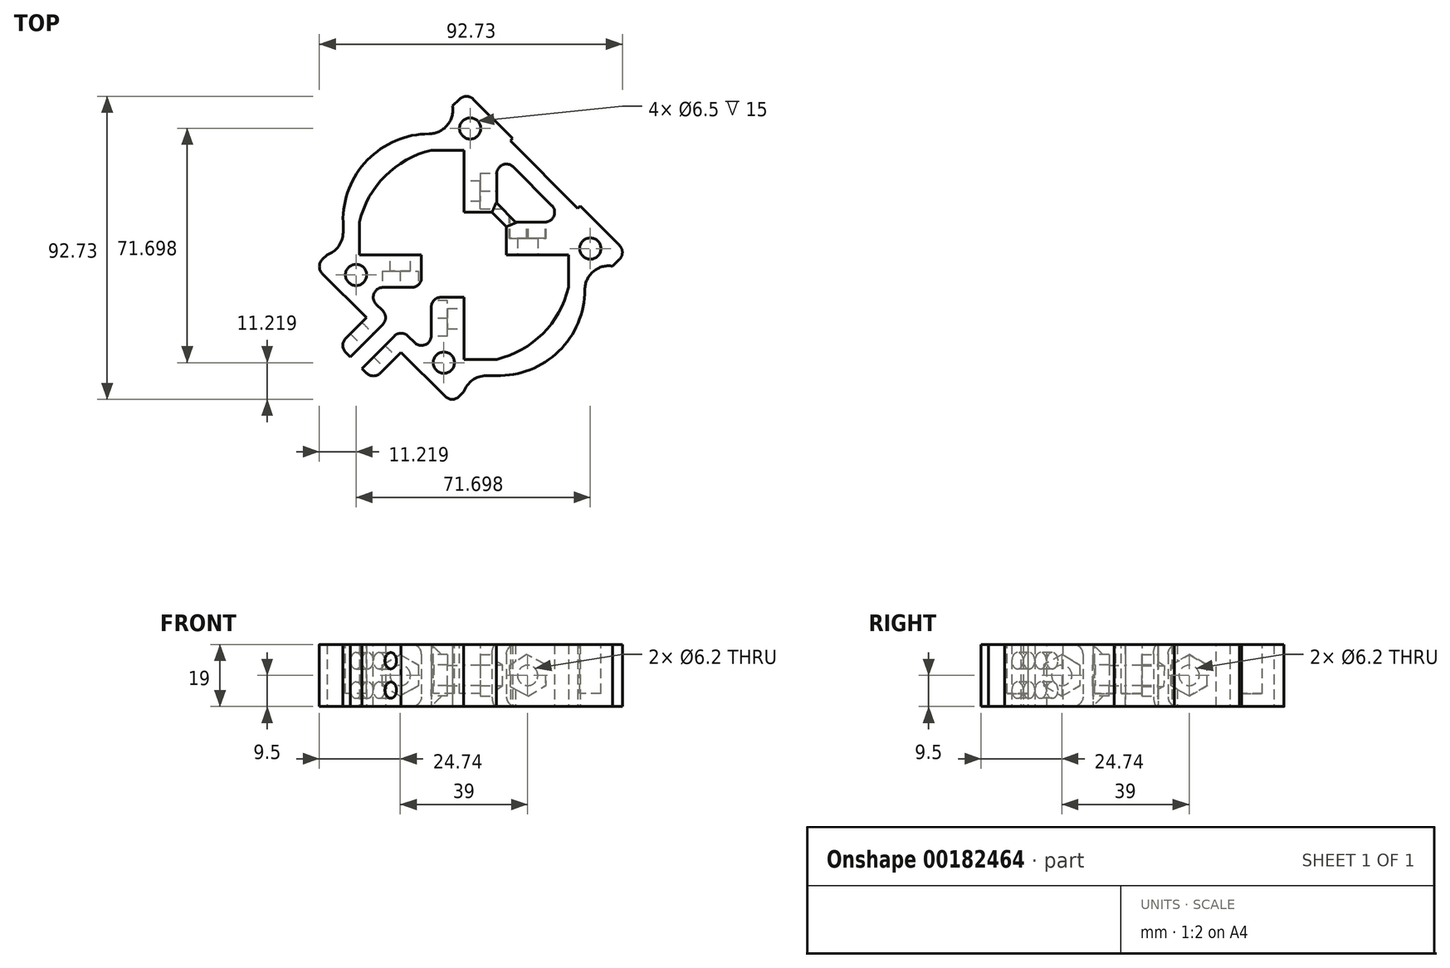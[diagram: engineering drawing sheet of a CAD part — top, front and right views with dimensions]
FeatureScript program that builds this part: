
annotation { "Feature Type Name" : "Feature", "Feature Type Description" : "" }
export const myFeature = defineFeature(function(context is Context, id is Id, definition is map)
    precondition{}
    {
        {
            var Q0;
            Q0=qCreatedBy(makeId("Top.planeOp"),FACE);
            var sketch = newSketch(context, id + "F0", { "sketchPlane" : qUnion([Q0])});
            skLineSegment(sketch, "E0.bottom", {"start": v(13, 13) * mm, "end": v(-13, 13) * mm, "construction": true});
            skLineSegment(sketch, "E0.top", {"start": v(13, -13) * mm, "end": v(-13, -13) * mm, "construction": true});
            skLineSegment(sketch, "E0.left", {"start": v(13, 13) * mm, "end": v(13, -13) * mm, "construction": true});
            skLineSegment(sketch, "E0.right", {"start": v(-13, 13) * mm, "end": v(-13, -13) * mm, "construction": true});
            skPoint(sketch, "E0.middle", {"position": v(0, 0) * mm});
            skLineSegment(sketch, "E1.bottom", {"start": v(13, 0) * mm, "end": v(32, 0) * mm});
            skLineSegment(sketch, "E1.top", {"start": v(13, 10) * mm, "end": v(32, 10) * mm});
            skLineSegment(sketch, "E1.left", {"start": v(13, 0) * mm, "end": v(13, 10) * mm});
            skLineSegment(sketch, "E1.right", {"start": v(32, 0) * mm, "end": v(32, 10) * mm});
            skLineSegment(sketch, "E2.bottom", {"start": v(0, 13) * mm, "end": v(10, 13) * mm});
            skLineSegment(sketch, "E2.top", {"start": v(0, 32) * mm, "end": v(10, 32) * mm});
            skLineSegment(sketch, "E2.left", {"start": v(0, 13) * mm, "end": v(0, 32) * mm});
            skLineSegment(sketch, "E2.right", {"start": v(10, 13) * mm, "end": v(10, 32) * mm});
            skLineSegment(sketch, "E3.bottom", {"start": v(0, -13) * mm, "end": v(-10, -13) * mm});
            skLineSegment(sketch, "E3.top", {"start": v(0, -32) * mm, "end": v(-10, -32) * mm});
            skLineSegment(sketch, "E3.left", {"start": v(0, -13) * mm, "end": v(0, -32) * mm});
            skLineSegment(sketch, "E3.right", {"start": v(-10, -13) * mm, "end": v(-10, -32) * mm});
            skLineSegment(sketch, "E4.bottom", {"start": v(-13, 0) * mm, "end": v(-32, 0) * mm});
            skLineSegment(sketch, "E4.top", {"start": v(-13, -10) * mm, "end": v(-32, -10) * mm});
            skLineSegment(sketch, "E4.left", {"start": v(-13, 0) * mm, "end": v(-13, -10) * mm});
            skLineSegment(sketch, "E4.right", {"start": v(-32, 0) * mm, "end": v(-32, -10) * mm});
            skLineSegment(sketch, "E5", {"start": v(32, 0) * mm, "end": v(32, -10) * mm});
            skLineSegment(sketch, "E6", {"start": v(0, -32) * mm, "end": v(10, -32) * mm});
            skLineSegment(sketch, "E7", {"start": v(-32, 0) * mm, "end": v(-32, 10) * mm});
            skLineSegment(sketch, "E8", {"start": v(0, 32) * mm, "end": v(-10, 32) * mm});
            skArc(sketch, "E9", {"start": v(10, -32) * mm, "mid": v(25.74, -25.74) * mm, "end": v(32, -10) * mm, "construction": true});
            skArc(sketch, "E10", {"start": v(-10, 32) * mm, "mid": v(-25.74, 25.74) * mm, "end": v(-32, 10) * mm, "construction": true});
            skCircle(sketch, "E11", {"center": v(0, 0) * mm, "radius": 15 * mm, "construction": true});
            skLineSegment(sketch, "E12", {"start": v(10, 32) * mm, "end": v(32, 10) * mm});
            skLineSegment(sketch, "E13", {"start": v(-32, -10) * mm, "end": v(-10, -32) * mm});
            skLineSegment(sketch, "E14.0", {"start": v(-37, 0) * mm, "end": v(-37, -12.07) * mm});
            skLineSegment(sketch, "E14.1", {"start": v(37, 0) * mm, "end": v(37, -9.93) * mm});
            skArc(sketch, "E14.2", {"start": v(9.93, -37) * mm, "mid": v(29.28, -29.28) * mm, "end": v(37, -9.93) * mm});
            skLineSegment(sketch, "E14.3", {"start": v(0, -37) * mm, "end": v(9.93, -37) * mm});
            skLineSegment(sketch, "E14.4", {"start": v(0, -37) * mm, "end": v(-12.07, -37) * mm});
            skLineSegment(sketch, "E14.5", {"start": v(37, 0) * mm, "end": v(37, 12.07) * mm});
            skLineSegment(sketch, "E14.6", {"start": v(-37, -12.07) * mm, "end": v(-12.07, -37) * mm});
            skLineSegment(sketch, "E14.7", {"start": v(12.07, 37) * mm, "end": v(37, 12.07) * mm});
            skLineSegment(sketch, "E14.8", {"start": v(0, 37) * mm, "end": v(12.07, 37) * mm});
            skLineSegment(sketch, "E14.9", {"start": v(0, 37) * mm, "end": v(-9.93, 37) * mm});
            skArc(sketch, "E14.10", {"start": v(-9.93, 37) * mm, "mid": v(-29.28, 29.28) * mm, "end": v(-37, 9.93) * mm});
            skLineSegment(sketch, "E14.11", {"start": v(-37, 0) * mm, "end": v(-37, 9.93) * mm});
            skCircle(sketch, "E15", {"center": v(0, 0) * mm, "radius": 4.5 * mm, "construction": true});
            skArc(sketch, "E16", {"start": v(-10, 32) * mm, "mid": v(-24.12, 24.12) * mm, "end": v(-32, 10) * mm});
            skArc(sketch, "E17", {"start": v(10, -32) * mm, "mid": v(24.12, -24.12) * mm, "end": v(32, -10) * mm});
            skLineSegment(sketch, "E18", {"start": v(10, 13) * mm, "end": v(13, 10) * mm, "construction": true});
            skLineSegment(sketch, "E19", {"start": v(10, 15.83) * mm, "end": v(15.83, 10) * mm});
            skLineSegment(sketch, "E20", {"start": v(8.59, 13) * mm, "end": v(13, 8.59) * mm});
            skLineSegment(sketch, "E21", {"start": v(-21, -21) * mm, "end": v(-32.77, -32.77) * mm, "construction": true});
            skLineSegment(sketch, "E22.0", {"start": v(-22.77, -19.23) * mm, "end": v(-34.79, -31.25) * mm});
            skLineSegment(sketch, "E23.0", {"start": v(-19.23, -22.77) * mm, "end": v(-31.25, -34.79) * mm});
            skLineSegment(sketch, "E24", {"start": v(-34.79, -31.25) * mm, "end": v(-38.32, -27.72) * mm});
            skLineSegment(sketch, "E25", {"start": v(-38.32, -27.72) * mm, "end": v(-29.84, -19.23) * mm});
            skLineSegment(sketch, "E26", {"start": v(-31.25, -34.79) * mm, "end": v(-27.72, -38.32) * mm});
            skLineSegment(sketch, "E27", {"start": v(-27.72, -38.32) * mm, "end": v(-19.23, -29.84) * mm});
            skLineSegment(sketch, "E28", {"start": v(37, 12.07) * mm, "end": v(49.02, 0.05) * mm});
            skLineSegment(sketch, "E29", {"start": v(49.02, 0.05) * mm, "end": v(45.49, -3.49) * mm});
            skLineSegment(sketch, "E30", {"start": v(45.49, -3.49) * mm, "end": v(32, 10) * mm});
            skLineSegment(sketch, "E31", {"start": v(12.07, 37) * mm, "end": v(0.05, 49.02) * mm});
            skLineSegment(sketch, "E32", {"start": v(0.05, 49.02) * mm, "end": v(-3.49, 45.49) * mm});
            skLineSegment(sketch, "E33", {"start": v(-3.49, 45.49) * mm, "end": v(10, 32) * mm});
            skLineSegment(sketch, "E34", {"start": v(-12.07, -37) * mm, "end": v(-3.59, -45.49) * mm});
            skLineSegment(sketch, "E35", {"start": v(-3.59, -45.49) * mm, "end": v(-0.05, -41.95) * mm});
            skLineSegment(sketch, "E36", {"start": v(-0.05, -41.95) * mm, "end": v(-10, -32) * mm});
            skLineSegment(sketch, "E37", {"start": v(-37, -12.07) * mm, "end": v(-45.49, -3.59) * mm});
            skLineSegment(sketch, "E38", {"start": v(-45.49, -3.59) * mm, "end": v(-41.95, -0.05) * mm});
            skLineSegment(sketch, "E39", {"start": v(-41.95, -0.05) * mm, "end": v(-32, -10) * mm});
            skSolve(sketch);
        }
        {
            var Q0;
            Q0=makeQuery(id+"F0.imprint","IMPRINT",FACE,{"disambiguationData":[TD([[makeQuery(id+"F0.imprint","IMPRINT",EDGE,{"derivedFrom":sQuery(id+"F0.wireOp",EDGE,"E1.right")}),-1.0]])]});
            var Q1;
            Q1=makeQuery(id+"F0.imprint","IMPRINT",FACE,{"disambiguationData":[TD([[makeQuery(id+"F0.imprint","IMPRINT",EDGE,{"derivedFrom":sQuery(id+"F0.wireOp",EDGE,"E3.bottom")}),1.0]])]});
            var Q2;
            Q2=makeQuery(id+"F0.imprint","IMPRINT",FACE,{"disambiguationData":[TD([[makeQuery(id+"F0.imprint","IMPRINT",EDGE,{"derivedFrom":sQuery(id+"F0.wireOp",EDGE,"E1.bottom")}),1.0]])]});
            var Q3;
            Q3=makeQuery(id+"F0.imprint","IMPRINT",FACE,{"disambiguationData":[TD([[makeQuery(id+"F0.imprint","IMPRINT",EDGE,{"derivedFrom":sQuery(id+"F0.wireOp",EDGE,"E2.bottom")}),1.0]])]});
            var Q4;
            Q4=makeQuery(id+"F0.imprint","IMPRINT",FACE,{"disambiguationData":[TD([[makeQuery(id+"F0.imprint","IMPRINT",EDGE,{"derivedFrom":sQuery(id+"F0.wireOp",EDGE,"E4.bottom")}),1.0]])]});
            var Q5;
            {var subQ4=sQuery(id+"F0.wireOp",EDGE,"E24");Q5=makeQuery(id+"F0.imprint","IMPRINT",FACE,{"disambiguationData":[TD([[makeQuery(id+"F0.imprint","IMPRINT",EDGE,{"derivedFrom":subQ4}),-1.0]])]});}
            var Q6;
            {var subQ4=sQuery(id+"F0.wireOp",EDGE,"E26");Q6=makeQuery(id+"F0.imprint","IMPRINT",FACE,{"disambiguationData":[TD([[makeQuery(id+"F0.imprint","IMPRINT",EDGE,{"derivedFrom":subQ4}),1.0]])]});}
            var Q7;
            {var subQ3=sQuery(id+"F0.wireOp",EDGE,"E19");Q7=makeQuery(id+"F0.imprint","IMPRINT",FACE,{"disambiguationData":[TD([[makeQuery(id+"F0.imprint","IMPRINT",EDGE,{"derivedFrom":subQ3}),-1.0]])]});}
            var Q8;
            {var subQ4=sQuery(id+"F0.wireOp",EDGE,"E12");Q8=makeQuery(id+"F0.imprint","IMPRINT",FACE,{"disambiguationData":[TD([[makeQuery(id+"F0.imprint","IMPRINT",EDGE,{"derivedFrom":subQ4}),1.0]])]});}
            var Q9;
            {var subQ0=sQuery(id+"F0.wireOp",EDGE,"E31");Q9=makeQuery(id+"F0.imprint","IMPRINT",FACE,{"disambiguationData":[TD([[makeQuery(id+"F0.imprint","IMPRINT",EDGE,{"derivedFrom":subQ0}),1.0]])]});}
            var Q10;
            {var subQ7=sQuery(id+"F0.wireOp",EDGE,"E2.top");Q10=makeQuery(id+"F0.imprint","IMPRINT",FACE,{"disambiguationData":[TD([[makeQuery(id+"F0.imprint","IMPRINT",EDGE,{"derivedFrom":subQ7}),1.0]])]});}
            var Q11;
            {var subQ0=sQuery(id+"F0.wireOp",EDGE,"E28");Q11=makeQuery(id+"F0.imprint","IMPRINT",FACE,{"disambiguationData":[TD([[makeQuery(id+"F0.imprint","IMPRINT",EDGE,{"derivedFrom":subQ0}),-1.0]])]});}
            var Q12;
            {var subQ0=sQuery(id+"F0.wireOp",EDGE,"E14.6");var subQ3=makeQuery(id+"F0.imprint","INTERSECT",VERTEX,{"derivedFrom":[subQ0,sQuery(id+"F0.wireOp",EDGE,"E27")]});Q12=makeQuery(id+"F0.imprint","IMPRINT",FACE,{"disambiguationData":[TD([[makeQuery(id+"F0.imprint","IMPRINT",EDGE,{"disambiguationData":[TD([[subQ3,1.0]])],"derivedFrom":subQ0}),1.0]])]});}
            var Q13;
            {var subQ0=sQuery(id+"F0.wireOp",EDGE,"E34");Q13=makeQuery(id+"F0.imprint","IMPRINT",FACE,{"disambiguationData":[TD([[makeQuery(id+"F0.imprint","IMPRINT",EDGE,{"derivedFrom":subQ0}),1.0]])]});}
            var Q14;
            {var subQ0=sQuery(id+"F0.wireOp",EDGE,"E37");Q14=makeQuery(id+"F0.imprint","IMPRINT",FACE,{"disambiguationData":[TD([[makeQuery(id+"F0.imprint","IMPRINT",EDGE,{"derivedFrom":subQ0}),-1.0]])]});}
            var Q15;
            {var subQ0=sQuery(id+"F0.wireOp",EDGE,"E14.6");var subQ1=makeQuery(id+"F0.imprint","INTERSECT",VERTEX,{"derivedFrom":[subQ0,sQuery(id+"F0.wireOp",EDGE,"E25")]});Q15=makeQuery(id+"F0.imprint","IMPRINT",FACE,{"disambiguationData":[TD([[makeQuery(id+"F0.imprint","IMPRINT",EDGE,{"disambiguationData":[TD([[subQ1,-1.0]])],"derivedFrom":subQ0}),1.0]])]});}
            extrude(context, id + "F1", {"entities" : qUnion([Q0, Q1, Q2, Q3, Q4, Q5, Q6, Q7, Q8, Q9, Q10, Q11, Q12, Q13, Q14, Q15]), "depth" : 19 * mm});
        }
        {
            var Q0;
            Q0=makeQuery(id+"F1.opExtrude","SWEPT_FACE",FACE,{"disambiguationData":[OSD([sQuery(id+"F0.wireOp",EDGE,"E3.right")])]});
            var sketch = newSketch(context, id + "F2", { "sketchPlane" : qUnion([Q0])});
            skLineSegment(sketch, "E40", {"start": v(19.5, 9.5) * mm, "end": v(32, 9.5) * mm, "construction": true});
            skCircle(sketch, "E41.cCircle", {"center": v(19.5, 9.5) * mm, "radius": 5.5 * mm, "construction": true});
            skLineSegment(sketch, "E41.0", {"start": v(14, 6.32) * mm, "end": v(14, 12.68) * mm});
            skLineSegment(sketch, "E41.1", {"start": v(14, 12.68) * mm, "end": v(19.5, 15.85) * mm});
            skLineSegment(sketch, "E41.2", {"start": v(19.5, 15.85) * mm, "end": v(25, 12.68) * mm});
            skLineSegment(sketch, "E41.3", {"start": v(25, 12.68) * mm, "end": v(25, 6.32) * mm});
            skLineSegment(sketch, "E41.4", {"start": v(25, 6.32) * mm, "end": v(19.5, 3.15) * mm});
            skLineSegment(sketch, "E41.5", {"start": v(19.5, 3.15) * mm, "end": v(14, 6.32) * mm});
            skPoint(sketch, "E41.0.midPoint", {"position": v(14, 9.5) * mm});
            skSolve(sketch);
        }
        {
            var Q0;
            Q0=makeQuery(id+"F2.imprint","IMPRINT",FACE,{"disambiguationData":[TD([[makeQuery(id+"F2.imprint","IMPRINT",EDGE,{"derivedFrom":sQuery(id+"F2.wireOp",EDGE,"E41.0")}),-1.0]])]});
            extrude(context, id + "F3", {"entities" : qUnion([Q0]), "operationType" : NewBodyOperationType.REMOVE, "oppositeDirection" : true, "depth" : 5 * mm});
        }
        {
            var Q0;
            Q0=makeQuery(id+"F1.opExtrude","SWEPT_FACE",FACE,{"disambiguationData":[OSD([sQuery(id+"F0.wireOp",EDGE,"E4.top")])]});
            var sketch = newSketch(context, id + "F4", { "sketchPlane" : qUnion([Q0])});
            skLineSegment(sketch, "E42", {"start": v(-32, 9.5) * mm, "end": v(-19.5, 9.5) * mm, "construction": true});
            skPoint(sketch, "E42.endSnap0", {"position": v(-32, 9.5) * mm});
            skCircle(sketch, "E43.cCircle", {"center": v(-19.5, 9.5) * mm, "radius": 5.5 * mm, "construction": true});
            skLineSegment(sketch, "E43.0", {"start": v(-14, 12.68) * mm, "end": v(-14, 6.32) * mm});
            skLineSegment(sketch, "E43.1", {"start": v(-14, 6.32) * mm, "end": v(-19.5, 3.15) * mm});
            skLineSegment(sketch, "E43.2", {"start": v(-19.5, 3.15) * mm, "end": v(-25, 6.32) * mm});
            skLineSegment(sketch, "E43.3", {"start": v(-25, 6.32) * mm, "end": v(-25, 12.68) * mm});
            skLineSegment(sketch, "E43.4", {"start": v(-25, 12.68) * mm, "end": v(-19.5, 15.85) * mm});
            skLineSegment(sketch, "E43.5", {"start": v(-19.5, 15.85) * mm, "end": v(-14, 12.68) * mm});
            skPoint(sketch, "E43.0.midPoint", {"position": v(-14, 9.5) * mm});
            skSolve(sketch);
        }
        {
            var Q0;
            Q0=makeQuery(id+"F4.imprint","IMPRINT",FACE,{"disambiguationData":[TD([[makeQuery(id+"F4.imprint","IMPRINT",EDGE,{"derivedFrom":sQuery(id+"F4.wireOp",EDGE,"E43.0")}),-1.0]])]});
            extrude(context, id + "F5", {"entities" : qUnion([Q0]), "operationType" : NewBodyOperationType.REMOVE, "oppositeDirection" : true, "depth" : 5 * mm});
        }
        {
            var Q0;
            Q0=makeQuery(id+"F1.opExtrude","SWEPT_FACE",FACE,{"disambiguationData":[OSD([sQuery(id+"F0.wireOp",EDGE,"E2.right")])]});
            var sketch = newSketch(context, id + "F6", { "sketchPlane" : qUnion([Q0])});
            skCircle(sketch, "E44.cCircle", {"center": v(19.5, 9.5) * mm, "radius": 5.5 * mm, "construction": true});
            skLineSegment(sketch, "E44.0", {"start": v(14, 6.32) * mm, "end": v(14, 12.68) * mm});
            skLineSegment(sketch, "E44.1", {"start": v(14, 12.68) * mm, "end": v(19.5, 15.85) * mm});
            skLineSegment(sketch, "E44.2", {"start": v(19.5, 15.85) * mm, "end": v(25, 12.68) * mm});
            skLineSegment(sketch, "E44.3", {"start": v(25, 12.68) * mm, "end": v(25, 6.32) * mm});
            skLineSegment(sketch, "E44.4", {"start": v(25, 6.32) * mm, "end": v(19.5, 3.15) * mm});
            skLineSegment(sketch, "E44.5", {"start": v(19.5, 3.15) * mm, "end": v(14, 6.32) * mm});
            skPoint(sketch, "E44.0.midPoint", {"position": v(14, 9.5) * mm});
            skSolve(sketch);
        }
        {
            var Q0;
            Q0=makeQuery(id+"F6.imprint","IMPRINT",FACE,{"disambiguationData":[TD([[makeQuery(id+"F6.imprint","IMPRINT",EDGE,{"derivedFrom":sQuery(id+"F6.wireOp",EDGE,"E44.0")}),-1.0]])]});
            var Q1;
            {var subQ1=sQuery(id+"F6.wireOp",EDGE,"E44.2");Q1=makeQuery(id+"F6.imprint","IMPRINT",FACE,{"disambiguationData":[TD([[makeQuery(id+"F6.imprint","IMPRINT",EDGE,{"derivedFrom":subQ1}),-1.0]])]});}
            extrude(context, id + "F7", {"entities" : qUnion([Q0, Q1]), "operationType" : NewBodyOperationType.REMOVE, "oppositeDirection" : true, "depth" : 10 * mm, "symmetric" : true});
        }
        {
            var Q0;
            Q0=makeQuery(id+"F1.opExtrude","SWEPT_FACE",FACE,{"disambiguationData":[OSD([sQuery(id+"F0.wireOp",EDGE,"E1.top")])]});
            var sketch = newSketch(context, id + "F8", { "sketchPlane" : qUnion([Q0])});
            skLineSegment(sketch, "E45", {"start": v(-32, 9.5) * mm, "end": v(-19.5, 9.5) * mm, "construction": true});
            skCircle(sketch, "E46.cCircle", {"center": v(-19.5, 9.5) * mm, "radius": 5.5 * mm, "construction": true});
            skLineSegment(sketch, "E46.0", {"start": v(-13.87, 12.45) * mm, "end": v(-14.13, 6.1) * mm});
            skLineSegment(sketch, "E46.1", {"start": v(-14.13, 6.1) * mm, "end": v(-19.76, 3.15) * mm});
            skLineSegment(sketch, "E46.2", {"start": v(-19.76, 3.15) * mm, "end": v(-25.13, 6.55) * mm});
            skLineSegment(sketch, "E46.3", {"start": v(-25.13, 6.55) * mm, "end": v(-24.87, 12.9) * mm});
            skLineSegment(sketch, "E46.4", {"start": v(-24.87, 12.9) * mm, "end": v(-19.24, 15.85) * mm});
            skLineSegment(sketch, "E46.5", {"start": v(-19.24, 15.85) * mm, "end": v(-13.87, 12.45) * mm});
            skPoint(sketch, "E46.0.midPoint", {"position": v(-14, 9.27) * mm});
            skSolve(sketch);
        }
        {
            var Q0;
            Q0=makeQuery(id+"F8.imprint","IMPRINT",FACE,{"disambiguationData":[TD([[makeQuery(id+"F8.imprint","IMPRINT",EDGE,{"derivedFrom":sQuery(id+"F8.wireOp",EDGE,"E46.0")}),-1.0]])]});
            var Q1;
            {var subQ6=sQuery(id+"F8.wireOp",EDGE,"E46.2");Q1=makeQuery(id+"F8.imprint","IMPRINT",FACE,{"disambiguationData":[TD([[makeQuery(id+"F8.imprint","IMPRINT",EDGE,{"derivedFrom":subQ6}),-1.0]])]});}
            extrude(context, id + "F9", {"entities" : qUnion([Q0, Q1]), "operationType" : NewBodyOperationType.REMOVE, "oppositeDirection" : true, "depth" : 10 * mm, "symmetric" : true});
        }
        {
            var Q0;
            Q0=sQuery(id+"F6.wireOp",VERTEX,"E44.cCircle.center");
            var Q1;
            Q1=sQuery(id+"F8.wireOp",VERTEX,"E45.end");
            var Q2;
            Q2=sQuery(id+"F2.wireOp",VERTEX,"E41.cCircle.center");
            var Q3;
            Q3=sQuery(id+"F4.wireOp",VERTEX,"E42.end");
            var Q4;
            Q4=makeQuery(id+"F1.opExtrude","SWEPT_BODY",BODY,{"disambiguationData":[OSD([sQuery(id+"F0.wireOp",EDGE,"E1.bottom"),sQuery(id+"F0.wireOp",EDGE,"E1.top"),sQuery(id+"F0.wireOp",EDGE,"E1.left"),sQuery(id+"F0.wireOp",EDGE,"E2.bottom"),sQuery(id+"F0.wireOp",EDGE,"E2.left"),sQuery(id+"F0.wireOp",EDGE,"E2.right"),sQuery(id+"F0.wireOp",EDGE,"E3.bottom"),sQuery(id+"F0.wireOp",EDGE,"E3.left"),sQuery(id+"F0.wireOp",EDGE,"E3.right"),sQuery(id+"F0.wireOp",EDGE,"E4.bottom"),sQuery(id+"F0.wireOp",EDGE,"E4.top"),sQuery(id+"F0.wireOp",EDGE,"E4.left"),sQuery(id+"F0.wireOp",EDGE,"E5"),sQuery(id+"F0.wireOp",EDGE,"E6"),sQuery(id+"F0.wireOp",EDGE,"E7"),sQuery(id+"F0.wireOp",EDGE,"E8"),sQuery(id+"F0.wireOp",EDGE,"E12"),sQuery(id+"F0.wireOp",EDGE,"E13"),sQuery(id+"F0.wireOp",EDGE,"E14.0"),sQuery(id+"F0.wireOp",EDGE,"E14.1"),sQuery(id+"F0.wireOp",EDGE,"E14.2"),sQuery(id+"F0.wireOp",EDGE,"E14.3"),sQuery(id+"F0.wireOp",EDGE,"E14.4"),sQuery(id+"F0.wireOp",EDGE,"E14.5"),sQuery(id+"F0.wireOp",EDGE,"E14.6"),sQuery(id+"F0.wireOp",EDGE,"E14.7"),sQuery(id+"F0.wireOp",EDGE,"E14.8"),sQuery(id+"F0.wireOp",EDGE,"E14.9"),sQuery(id+"F0.wireOp",EDGE,"E14.10"),sQuery(id+"F0.wireOp",EDGE,"E14.11"),sQuery(id+"F0.wireOp",EDGE,"E16"),sQuery(id+"F0.wireOp",EDGE,"E17"),sQuery(id+"F0.wireOp",EDGE,"E19"),sQuery(id+"F0.wireOp",EDGE,"E20"),sQuery(id+"F0.wireOp",EDGE,"E22.0"),sQuery(id+"F0.wireOp",EDGE,"E23.0"),sQuery(id+"F0.wireOp",EDGE,"E24"),sQuery(id+"F0.wireOp",EDGE,"E25"),sQuery(id+"F0.wireOp",EDGE,"E26"),sQuery(id+"F0.wireOp",EDGE,"E27"),sQuery(id+"F0.wireOp",EDGE,"E28"),sQuery(id+"F0.wireOp",EDGE,"E29"),sQuery(id+"F0.wireOp",EDGE,"E30"),sQuery(id+"F0.wireOp",EDGE,"E31"),sQuery(id+"F0.wireOp",EDGE,"E32"),sQuery(id+"F0.wireOp",EDGE,"E33")])]});
            hole(context, id + "F10", {"style" : HoleStyle.SIMPLE, "endStyle" : HoleEndStyle.BLIND, "holeDiameter" : 6.2 * mm, "holeDepth" : 10 * mm, "locations" : qUnion([Q0, Q1, Q2, Q3]), "scope" : qUnion([Q4])});
        }
        {
            var Q0;
            Q0=makeQuery(id+"F1.opExtrude","SWEPT_FACE",FACE,{"disambiguationData":[OSD([sQuery(id+"F0.wireOp",EDGE,"E25")])]});
            var sketch = newSketch(context, id + "F11", { "sketchPlane" : qUnion([Q0])});
            skLineSegment(sketch, "E47", {"start": v(39.2, 0) * mm, "end": v(39.2, 19) * mm, "construction": true});
            skPoint(sketch, "E48", {"position": v(39.2, 5) * mm});
            skPoint(sketch, "E49", {"position": v(39.2, 14) * mm});
            skSolve(sketch);
        }
        {
            var Q0;
            Q0=sQuery(id+"F11.wireOp",VERTEX,"E49");
            var Q1;
            Q1=sQuery(id+"F11.wireOp",VERTEX,"E48");
            var Q2;
            Q2=makeQuery(id+"F1.opExtrude","SWEPT_BODY",BODY,{"disambiguationData":[OSD([sQuery(id+"F0.wireOp",EDGE,"E1.bottom"),sQuery(id+"F0.wireOp",EDGE,"E1.top"),sQuery(id+"F0.wireOp",EDGE,"E1.left"),sQuery(id+"F0.wireOp",EDGE,"E2.bottom"),sQuery(id+"F0.wireOp",EDGE,"E2.left"),sQuery(id+"F0.wireOp",EDGE,"E2.right"),sQuery(id+"F0.wireOp",EDGE,"E3.bottom"),sQuery(id+"F0.wireOp",EDGE,"E3.left"),sQuery(id+"F0.wireOp",EDGE,"E3.right"),sQuery(id+"F0.wireOp",EDGE,"E4.bottom"),sQuery(id+"F0.wireOp",EDGE,"E4.top"),sQuery(id+"F0.wireOp",EDGE,"E4.left"),sQuery(id+"F0.wireOp",EDGE,"E5"),sQuery(id+"F0.wireOp",EDGE,"E6"),sQuery(id+"F0.wireOp",EDGE,"E7"),sQuery(id+"F0.wireOp",EDGE,"E8"),sQuery(id+"F0.wireOp",EDGE,"E12"),sQuery(id+"F0.wireOp",EDGE,"E13"),sQuery(id+"F0.wireOp",EDGE,"E14.0"),sQuery(id+"F0.wireOp",EDGE,"E14.1"),sQuery(id+"F0.wireOp",EDGE,"E14.2"),sQuery(id+"F0.wireOp",EDGE,"E14.3"),sQuery(id+"F0.wireOp",EDGE,"E14.4"),sQuery(id+"F0.wireOp",EDGE,"E14.5"),sQuery(id+"F0.wireOp",EDGE,"E14.6"),sQuery(id+"F0.wireOp",EDGE,"E14.7"),sQuery(id+"F0.wireOp",EDGE,"E14.8"),sQuery(id+"F0.wireOp",EDGE,"E14.9"),sQuery(id+"F0.wireOp",EDGE,"E14.10"),sQuery(id+"F0.wireOp",EDGE,"E14.11"),sQuery(id+"F0.wireOp",EDGE,"E16"),sQuery(id+"F0.wireOp",EDGE,"E17"),sQuery(id+"F0.wireOp",EDGE,"E19"),sQuery(id+"F0.wireOp",EDGE,"E20"),sQuery(id+"F0.wireOp",EDGE,"E22.0"),sQuery(id+"F0.wireOp",EDGE,"E23.0"),sQuery(id+"F0.wireOp",EDGE,"E24"),sQuery(id+"F0.wireOp",EDGE,"E25"),sQuery(id+"F0.wireOp",EDGE,"E26"),sQuery(id+"F0.wireOp",EDGE,"E27"),sQuery(id+"F0.wireOp",EDGE,"E28"),sQuery(id+"F0.wireOp",EDGE,"E29"),sQuery(id+"F0.wireOp",EDGE,"E30"),sQuery(id+"F0.wireOp",EDGE,"E31"),sQuery(id+"F0.wireOp",EDGE,"E32"),sQuery(id+"F0.wireOp",EDGE,"E33")])]});
            hole(context, id + "F12", {"style" : HoleStyle.SIMPLE, "endStyle" : HoleEndStyle.BLIND, "holeDiameter" : 5 * mm, "holeDepth" : 15 * mm, "locations" : qUnion([Q0, Q1]), "scope" : qUnion([Q2])});
        }
        {
            var Q0;
            Q0=makeQuery(id+"F1.opExtrude","SWEPT_FACE",FACE,{"disambiguationData":[OSD([sQuery(id+"F0.wireOp",EDGE,"E14.7"),sQuery(id+"F0.wireOp",EDGE,"E28"),sQuery(id+"F0.wireOp",EDGE,"E31")])]});
            var sketch = newSketch(context, id + "F13", { "sketchPlane" : qUnion([Q0])});
            skLineSegment(sketch, "E50", {"start": v(-34.63, 19) * mm, "end": v(-34.63, 0) * mm});
            skLineSegment(sketch, "E51", {"start": v(34.63, 0) * mm, "end": v(34.63, 19) * mm});
            skLineSegment(sketch, "E52", {"start": v(-14.63, 19) * mm, "end": v(-14.63, 0) * mm});
            skLineSegment(sketch, "E53", {"start": v(14.63, 19) * mm, "end": v(14.63, 0) * mm});
            skSolve(sketch);
        }
        {
            var Q0;
            {var subQ0=sQuery(id+"F13.wireOp",EDGE,"E51");Q0=makeQuery(id+"F13.imprint","IMPRINT",FACE,{"disambiguationData":[TD([[makeQuery(id+"F13.imprint","IMPRINT",EDGE,{"derivedFrom":subQ0}),-1.0]])]});}
            var Q1;
            {var subQ0=sQuery(id+"F13.wireOp",EDGE,"E50");Q1=makeQuery(id+"F13.imprint","IMPRINT",FACE,{"disambiguationData":[TD([[makeQuery(id+"F13.imprint","IMPRINT",EDGE,{"derivedFrom":subQ0}),1.0]])]});}
            extrude(context, id + "F14", {"entities" : qUnion([Q0, Q1]), "operationType" : NewBodyOperationType.ADD, "depth" : 1 * mm});
        }
        {
            var Q0;
            Q0=makeQuery(id+"F1.opExtrude","SWEPT_EDGE",EDGE,{"disambiguationData":[OSD([sQuery(id+"F0.wireOp",EDGE,"E14.8"),sQuery(id+"F0.wireOp",EDGE,"E33")])]});
            var Q1;
            Q1=makeQuery(id+"F1.opExtrude","SWEPT_EDGE",EDGE,{"disambiguationData":[OSD([sQuery(id+"F0.wireOp",EDGE,"E14.5"),sQuery(id+"F0.wireOp",EDGE,"E30")])]});
            var Q2;
            Q2=makeQuery(id+"F14.opExtrude","CAP_EDGE",EDGE,{"disambiguationData":[OSD([sQuery(id+"F13.wireOp",EDGE,"E53")])],"isStart":true});
            var Q3;
            Q3=makeQuery(id+"F14.opExtrude","CAP_EDGE",EDGE,{"disambiguationData":[OSD([sQuery(id+"F13.wireOp",EDGE,"E52")])],"isStart":true});
            var Q4;
            Q4=makeQuery(id+"F1.opExtrude","SWEPT_EDGE",EDGE,{"disambiguationData":[OSD([sQuery(id+"F0.wireOp",EDGE,"E14.4"),sQuery(id+"F0.wireOp",EDGE,"E36")])]});
            var Q5;
            Q5=makeQuery(id+"F1.opExtrude","SWEPT_EDGE",EDGE,{"disambiguationData":[OSD([sQuery(id+"F0.wireOp",EDGE,"E14.0"),sQuery(id+"F0.wireOp",EDGE,"E39")])]});
            fillet(context, id + "F15", {"entities" : qUnion([Q0, Q1, Q2, Q3, Q4, Q5]), "radius" : 7.3 * mm, "tangentPropagation" : true, "allowEdgeOverflow" : false});
        }
        {
            var Q0;
            Q0=makeQuery(id+"F1.opExtrude","CAP_EDGE",EDGE,{"disambiguationData":[OSD([sQuery(id+"F0.wireOp",EDGE,"E4.left")])],"isStart":true});
            var Q1;
            Q1=makeQuery(id+"F1.opExtrude","CAP_EDGE",EDGE,{"disambiguationData":[OSD([sQuery(id+"F0.wireOp",EDGE,"E3.bottom")])],"isStart":false});
            var Q2;
            Q2=makeQuery(id+"F1.opExtrude","CAP_EDGE",EDGE,{"disambiguationData":[OSD([sQuery(id+"F0.wireOp",EDGE,"E4.left")])],"isStart":false});
            var Q3;
            Q3=makeQuery(id+"F1.opExtrude","CAP_EDGE",EDGE,{"disambiguationData":[OSD([sQuery(id+"F0.wireOp",EDGE,"E3.bottom")])],"isStart":true});
            var Q4;
            Q4=makeQuery(id+"F1.opExtrude","CAP_EDGE",EDGE,{"disambiguationData":[OSD([sQuery(id+"F0.wireOp",EDGE,"E2.bottom")])],"isStart":false});
            var Q5;
            Q5=makeQuery(id+"F1.opExtrude","CAP_EDGE",EDGE,{"disambiguationData":[OSD([sQuery(id+"F0.wireOp",EDGE,"E20")])],"isStart":false});
            var Q6;
            Q6=makeQuery(id+"F1.opExtrude","CAP_EDGE",EDGE,{"disambiguationData":[OSD([sQuery(id+"F0.wireOp",EDGE,"E1.left")])],"isStart":false});
            var Q7;
            Q7=makeQuery(id+"F1.opExtrude","CAP_EDGE",EDGE,{"disambiguationData":[OSD([sQuery(id+"F0.wireOp",EDGE,"E1.left")])],"isStart":true});
            var Q8;
            Q8=makeQuery(id+"F1.opExtrude","CAP_EDGE",EDGE,{"disambiguationData":[OSD([sQuery(id+"F0.wireOp",EDGE,"E20")])],"isStart":true});
            var Q9;
            {var subQ0=sQuery(id+"F13.wireOp",EDGE,"E52");Q9=makeQuery(id+"F15.opFillet","BLEND_EDGE",EDGE,{"blendedFrom":[makeQuery(id+"F14.opExtrude","CAP_EDGE",EDGE,{"disambiguationData":[OSD([subQ0])],"isStart":true}),makeQuery(id+"F14.opExtrude","CAP_FACE",FACE,{"disambiguationData":[OSD([sQuery(id+"F0.wireOp",EDGE,"E14.7"),sQuery(id+"F0.wireOp",EDGE,"E28"),sQuery(id+"F0.wireOp",EDGE,"E31"),sQuery(id+"F13.wireOp",EDGE,"E50"),subQ0])],"isStart":false})],"blendedInto":[makeQuery(id+"F14.opExtrude","CAP_FACE",FACE,{"disambiguationData":[OSD([sQuery(id+"F0.wireOp",EDGE,"E14.7"),sQuery(id+"F0.wireOp",EDGE,"E28"),sQuery(id+"F0.wireOp",EDGE,"E31"),sQuery(id+"F13.wireOp",EDGE,"E50"),subQ0])],"isStart":false})]});}
            var Q10;
            {var subQ0=sQuery(id+"F13.wireOp",EDGE,"E53");Q10=makeQuery(id+"F15.opFillet","BLEND_EDGE",EDGE,{"blendedFrom":[makeQuery(id+"F14.opExtrude","CAP_EDGE",EDGE,{"disambiguationData":[OSD([subQ0])],"isStart":true}),makeQuery(id+"F14.opExtrude","CAP_FACE",FACE,{"disambiguationData":[OSD([sQuery(id+"F0.wireOp",EDGE,"E14.7"),sQuery(id+"F0.wireOp",EDGE,"E28"),sQuery(id+"F0.wireOp",EDGE,"E31"),sQuery(id+"F13.wireOp",EDGE,"E51"),subQ0])],"isStart":false})],"blendedInto":[makeQuery(id+"F14.opExtrude","CAP_FACE",FACE,{"disambiguationData":[OSD([sQuery(id+"F0.wireOp",EDGE,"E14.7"),sQuery(id+"F0.wireOp",EDGE,"E28"),sQuery(id+"F0.wireOp",EDGE,"E31"),sQuery(id+"F13.wireOp",EDGE,"E51"),subQ0])],"isStart":false})]});}
            var Q11;
            Q11=makeQuery(id+"F1.opExtrude","SWEPT_EDGE",EDGE,{"disambiguationData":[OSD([sQuery(id+"F0.wireOp",EDGE,"E24"),sQuery(id+"F0.wireOp",EDGE,"E25")])]});
            var Q12;
            Q12=makeQuery(id+"F1.opExtrude","SWEPT_EDGE",EDGE,{"disambiguationData":[OSD([sQuery(id+"F0.wireOp",EDGE,"E26"),sQuery(id+"F0.wireOp",EDGE,"E27")])]});
            var Q13;
            Q13=makeQuery(id+"F1.opExtrude","SWEPT_EDGE",EDGE,{"disambiguationData":[OSD([sQuery(id+"F0.wireOp",EDGE,"E4.top"),sQuery(id+"F0.wireOp",EDGE,"E4.left")])]});
            var Q14;
            Q14=makeQuery(id+"F1.opExtrude","SWEPT_EDGE",EDGE,{"disambiguationData":[OSD([sQuery(id+"F0.wireOp",EDGE,"E3.bottom"),sQuery(id+"F0.wireOp",EDGE,"E3.right")])]});
            var Q15;
            Q15=makeQuery(id+"F1.opExtrude","SWEPT_EDGE",EDGE,{"disambiguationData":[OSD([sQuery(id+"F0.wireOp",EDGE,"E13"),sQuery(id+"F0.wireOp",EDGE,"E22.0")])]});
            var Q16;
            Q16=makeQuery(id+"F1.opExtrude","SWEPT_EDGE",EDGE,{"disambiguationData":[OSD([sQuery(id+"F0.wireOp",EDGE,"E13"),sQuery(id+"F0.wireOp",EDGE,"E23.0")])]});
            var Q17;
            Q17=makeQuery(id+"F14.opExtrude","CAP_EDGE",EDGE,{"disambiguationData":[OSD([sQuery(id+"F13.wireOp",EDGE,"E51")])],"isStart":false});
            var Q18;
            Q18=makeQuery(id+"F14.opExtrude","CAP_EDGE",EDGE,{"disambiguationData":[OSD([sQuery(id+"F13.wireOp",EDGE,"E50")])],"isStart":false});
            var Q19;
            Q19=makeQuery(id+"F1.opExtrude","SWEPT_EDGE",EDGE,{"disambiguationData":[OSD([sQuery(id+"F0.wireOp",EDGE,"E34"),sQuery(id+"F0.wireOp",EDGE,"E35")])]});
            var Q20;
            Q20=makeQuery(id+"F1.opExtrude","SWEPT_EDGE",EDGE,{"disambiguationData":[OSD([sQuery(id+"F0.wireOp",EDGE,"E37"),sQuery(id+"F0.wireOp",EDGE,"E38")])]});
            var Q21;
            Q21=makeQuery(id+"F1.opExtrude","SWEPT_EDGE",EDGE,{"disambiguationData":[OSD([sQuery(id+"F0.wireOp",EDGE,"E3.top"),sQuery(id+"F0.wireOp",EDGE,"E3.right"),sQuery(id+"F0.wireOp",EDGE,"E13"),sQuery(id+"F0.wireOp",EDGE,"E36")])]});
            var Q22;
            Q22=makeQuery(id+"F1.opExtrude","SWEPT_EDGE",EDGE,{"disambiguationData":[OSD([sQuery(id+"F0.wireOp",EDGE,"E4.top"),sQuery(id+"F0.wireOp",EDGE,"E4.right"),sQuery(id+"F0.wireOp",EDGE,"E13"),sQuery(id+"F0.wireOp",EDGE,"E39")])]});
            var Q23;
            Q23=makeQuery(id+"F1.opExtrude","SWEPT_EDGE",EDGE,{"disambiguationData":[OSD([sQuery(id+"F0.wireOp",EDGE,"E2.top"),sQuery(id+"F0.wireOp",EDGE,"E2.right"),sQuery(id+"F0.wireOp",EDGE,"E12"),sQuery(id+"F0.wireOp",EDGE,"E33")])]});
            var Q24;
            Q24=makeQuery(id+"F1.opExtrude","SWEPT_EDGE",EDGE,{"disambiguationData":[OSD([sQuery(id+"F0.wireOp",EDGE,"E1.top"),sQuery(id+"F0.wireOp",EDGE,"E1.right"),sQuery(id+"F0.wireOp",EDGE,"E12"),sQuery(id+"F0.wireOp",EDGE,"E30")])]});
            var Q25;
            Q25=makeQuery(id+"F1.opExtrude","CAP_EDGE",EDGE,{"disambiguationData":[OSD([sQuery(id+"F0.wireOp",EDGE,"E2.bottom")])],"isStart":true});
            fillet(context, id + "F16", {"entities" : qUnion([Q0, Q1, Q2, Q3, Q4, Q5, Q6, Q7, Q8, Q9, Q10, Q11, Q12, Q13, Q14, Q15, Q16, Q17, Q18, Q19, Q20, Q21, Q22, Q23, Q24, Q25]), "radius" : 3 * mm, "tangentPropagation" : true, "allowEdgeOverflow" : false});
        }
        {
            var Q0;
            {var subQ0=sQuery(id+"F0.wireOp",EDGE,"E31");var subQ1=sQuery(id+"F0.wireOp",EDGE,"E28");var subQ2=sQuery(id+"F0.wireOp",EDGE,"E14.7");var subQ3=makeQuery(id+"F1.opExtrude","CAP_EDGE",EDGE,{"disambiguationData":[OSD([subQ2,subQ1,subQ0])],"isStart":false});Q0=makeQuery(id+"F14.boolean.opBoolean","MERGE",FACE,{"derivedFrom":[makeQuery(id+"F1.opExtrude","CAP_FACE",FACE,{"disambiguationData":[OSD([sQuery(id+"F0.wireOp",EDGE,"E1.bottom"),sQuery(id+"F0.wireOp",EDGE,"E1.top"),sQuery(id+"F0.wireOp",EDGE,"E1.left"),sQuery(id+"F0.wireOp",EDGE,"E2.bottom"),sQuery(id+"F0.wireOp",EDGE,"E2.left"),sQuery(id+"F0.wireOp",EDGE,"E2.right"),sQuery(id+"F0.wireOp",EDGE,"E3.bottom"),sQuery(id+"F0.wireOp",EDGE,"E3.left"),sQuery(id+"F0.wireOp",EDGE,"E3.right"),sQuery(id+"F0.wireOp",EDGE,"E4.bottom"),sQuery(id+"F0.wireOp",EDGE,"E4.top"),sQuery(id+"F0.wireOp",EDGE,"E4.left"),sQuery(id+"F0.wireOp",EDGE,"E5"),sQuery(id+"F0.wireOp",EDGE,"E6"),sQuery(id+"F0.wireOp",EDGE,"E7"),sQuery(id+"F0.wireOp",EDGE,"E8"),sQuery(id+"F0.wireOp",EDGE,"E12"),sQuery(id+"F0.wireOp",EDGE,"E13"),sQuery(id+"F0.wireOp",EDGE,"E14.0"),sQuery(id+"F0.wireOp",EDGE,"E14.1"),sQuery(id+"F0.wireOp",EDGE,"E14.2"),sQuery(id+"F0.wireOp",EDGE,"E14.3"),sQuery(id+"F0.wireOp",EDGE,"E14.4"),sQuery(id+"F0.wireOp",EDGE,"E14.5"),sQuery(id+"F0.wireOp",EDGE,"E14.6"),subQ2,sQuery(id+"F0.wireOp",EDGE,"E14.8"),sQuery(id+"F0.wireOp",EDGE,"E14.9"),sQuery(id+"F0.wireOp",EDGE,"E14.10"),sQuery(id+"F0.wireOp",EDGE,"E14.11"),sQuery(id+"F0.wireOp",EDGE,"E16"),sQuery(id+"F0.wireOp",EDGE,"E17"),sQuery(id+"F0.wireOp",EDGE,"E19"),sQuery(id+"F0.wireOp",EDGE,"E20"),sQuery(id+"F0.wireOp",EDGE,"E22.0"),sQuery(id+"F0.wireOp",EDGE,"E23.0"),sQuery(id+"F0.wireOp",EDGE,"E24"),sQuery(id+"F0.wireOp",EDGE,"E25"),sQuery(id+"F0.wireOp",EDGE,"E26"),sQuery(id+"F0.wireOp",EDGE,"E27"),subQ1,sQuery(id+"F0.wireOp",EDGE,"E29"),sQuery(id+"F0.wireOp",EDGE,"E30"),subQ0,sQuery(id+"F0.wireOp",EDGE,"E32"),sQuery(id+"F0.wireOp",EDGE,"E33")])],"isStart":false}),makeQuery(id+"F14.opExtrude","SWEPT_FACE",FACE,{"disambiguationData":[OSD([subQ2,subQ1,subQ0]),TDD([makeQuery(id+"F13.imprint","IMPRINT",EDGE,{"disambiguationData":[TD([[makeQuery(id+"F13.imprint","INTERSECT",VERTEX,{"derivedFrom":[subQ3,sQuery(id+"F13.wireOp",EDGE,"E50")]}),1.0]])],"derivedFrom":subQ3})])]}),makeQuery(id+"F14.opExtrude","SWEPT_FACE",FACE,{"disambiguationData":[OSD([subQ2,subQ1,subQ0]),TDD([makeQuery(id+"F13.imprint","IMPRINT",EDGE,{"disambiguationData":[TD([[makeQuery(id+"F13.imprint","INTERSECT",VERTEX,{"derivedFrom":[subQ3,sQuery(id+"F13.wireOp",EDGE,"E51")]}),-1.0]])],"derivedFrom":subQ3})])]})]});}
            var sketch = newSketch(context, id + "F17", { "sketchPlane" : qUnion([Q0])});
            skLineSegment(sketch, "E54", {"start": v(38.68, -0.55) * mm, "end": v(38.68, 4.37) * mm, "construction": true});
            skLineSegment(sketch, "E55", {"start": v(-0.55, 38.68) * mm, "end": v(4.37, 38.68) * mm, "construction": true});
            skCircle(sketch, "E56", {"center": v(1.9, 38.68) * mm, "radius": 3.25 * mm});
            skCircle(sketch, "E57", {"center": v(38.68, 1.9) * mm, "radius": 3.25 * mm});
            skLineSegment(sketch, "E58", {"start": v(1.9, 38.68) * mm, "end": v(-42.92, -6.15) * mm, "construction": true});
            skLineSegment(sketch, "E59", {"start": v(38.68, 1.9) * mm, "end": v(-6.15, -42.92) * mm, "construction": true});
            skLineSegment(sketch, "E60", {"start": v(-29.84, -19.23) * mm, "end": v(-6.15, -42.92) * mm, "construction": true});
            skLineSegment(sketch, "E61", {"start": v(-29.84, -19.23) * mm, "end": v(-42.92, -6.15) * mm, "construction": true});
            skCircle(sketch, "E62", {"center": v(-6.15, -33.02) * mm, "radius": 3.25 * mm});
            skCircle(sketch, "E63", {"center": v(-33.02, -6.15) * mm, "radius": 3.25 * mm});
            skLineSegment(sketch, "E64.0", {"start": v(33.73, 6.86) * mm, "end": v(-11.1, -37.97) * mm, "construction": true});
            skLineSegment(sketch, "E65.0", {"start": v(6.86, 33.73) * mm, "end": v(-37.97, -11.1) * mm, "construction": true});
            skSolve(sketch);
        }
        {
            var Q0;
            Q0=makeQuery(id+"F17.imprint","IMPRINT",FACE,{"disambiguationData":[TD([[makeQuery(id+"F17.imprint","IMPRINT",EDGE,{"derivedFrom":sQuery(id+"F17.wireOp",EDGE,"E57")}),1.0]])]});
            var Q1;
            Q1=makeQuery(id+"F17.imprint","IMPRINT",FACE,{"disambiguationData":[TD([[makeQuery(id+"F17.imprint","IMPRINT",EDGE,{"derivedFrom":sQuery(id+"F17.wireOp",EDGE,"E56")}),1.0]])]});
            var Q2;
            Q2=makeQuery(id+"F17.imprint","IMPRINT",FACE,{"disambiguationData":[TD([[makeQuery(id+"F17.imprint","IMPRINT",EDGE,{"derivedFrom":sQuery(id+"F17.wireOp",EDGE,"E62")}),1.0]])]});
            var Q3;
            Q3=makeQuery(id+"F17.imprint","IMPRINT",FACE,{"disambiguationData":[TD([[makeQuery(id+"F17.imprint","IMPRINT",EDGE,{"derivedFrom":sQuery(id+"F17.wireOp",EDGE,"E63")}),1.0]])]});
            extrude(context, id + "F18", {"entities" : qUnion([Q0, Q1, Q2, Q3]), "operationType" : NewBodyOperationType.REMOVE, "oppositeDirection" : true, "depth" : 15 * mm});
        }
    });
